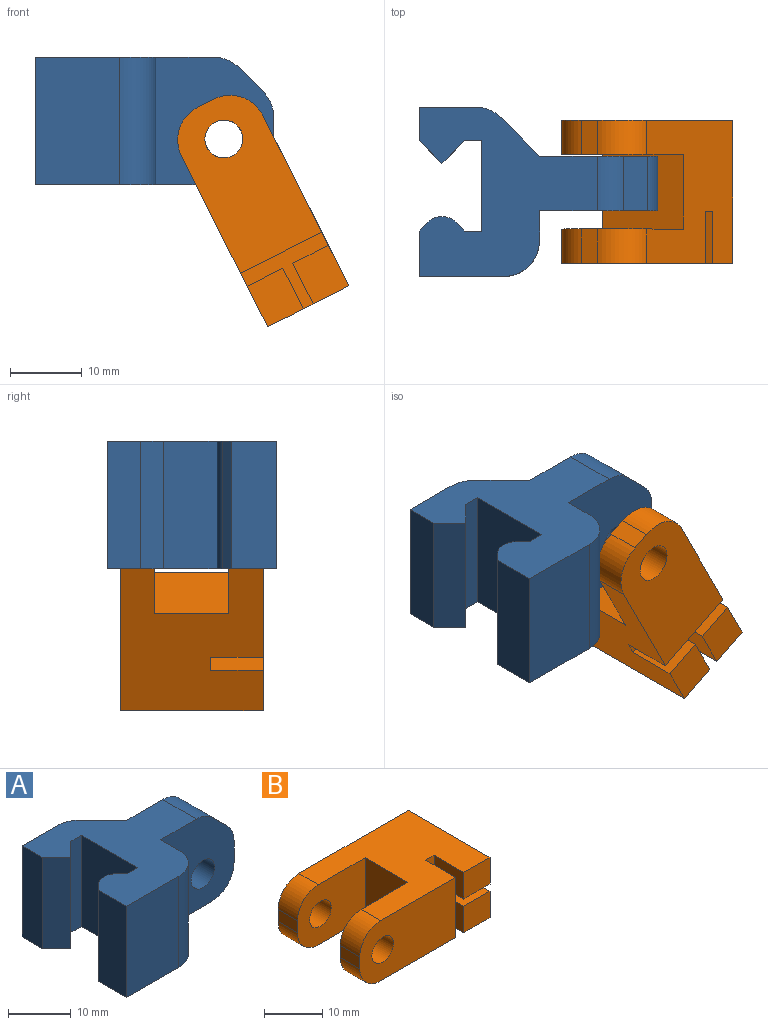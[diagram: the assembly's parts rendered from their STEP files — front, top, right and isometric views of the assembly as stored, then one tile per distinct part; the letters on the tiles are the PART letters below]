
ASSEMBLY  parts=2 mates=1
PART A: 26 faces, bbox 33.3x23.6x17.8 mm
  f0: plane 17.78x6.35mm, normal (-1,0,0), area 112.9mm2, adj f1,f12,f13,f14
  f1: plane 17.78x11.73mm, normal (0,-1,0), area 208.6mm2, adj f0,f13,f14,f23
  f2: plane 17.78x4.11mm, normal (1,0,0), area 73.1mm2, adj f13,f14,f15,f23
  f3: plane 17.78x5.33mm, normal (0.71,0.71,0), area 133.9mm2, adj f13,f14,f16,f21
  f4: plane 17.78x7.89mm, normal (0,1,0), area 140.3mm2, adj f5,f13,f14,f21
  f5: plane 17.78x4.64mm, normal (-1,0,0), area 82.4mm2, adj f4,f6,f13,f14
  f6: plane 17.78x3.18mm, normal (-0.71,-0.71,0), area 80mm2, adj f5,f7,f13,f14
  f7: plane 17.78x3.18mm, normal (0.71,-0.71,0), area 80mm2, adj f6,f8,f13,f14
  f8: plane 17.78x2.38mm, normal (0,-1,0), area 42.3mm2, adj f7,f9,f13,f14
  f9: plane 17.78x12.64mm, normal (-1,0,0), area 224.7mm2, adj f8,f10,f13,f14
  f10: plane 17.78x2.38mm, normal (0,1,0), area 42.3mm2, adj f9,f11,f13,f14
  f11: plane 17.78x1.21mm, normal (0.71,0.71,0), area 30.3mm2, adj f10,f13,f14,f20
  f12: plane 17.78x1.21mm, normal (-0.71,0.71,0), area 30.3mm2, adj f0,f13,f14,f20
  f13: plane 24.87x23.62mm, normal (0,0,1), area 337.2mm2, adj f0,f1,f2,f3,f4,f5,f6,f7
  f14: plane 28.24x23.62mm, normal (0,0,-1), area 362.9mm2, adj f0,f1,f2,f3,f4,f5,f6,f7
  f15: plane 17.78x16.51mm, normal (0,-1,0), area 244.7mm2, adj f2,f13,f14,f17,f18,f19,f22,f24
  f16: plane 17.78x16.51mm, normal (0,1,0), area 244.7mm2, adj f3,f13,f14,f17,f18,f19,f22,f24
  f17: plane 7.62x4.25mm, normal (1,0,0), area 32.4mm2, adj f15,f16,f22,f25
  f18: plane 7.62x3.37mm, normal (0.71,0,0.71), area 36.4mm2, adj f15,f16,f24,f25
  f19: cylinder r=2.65mm len=7.62mm, axis (0,-1,0), area 126.9mm2, adj f15,f16
  f20: cylinder r=2.79mm len=17.78mm, axis (0,0,-1), area 78mm2, adj f11,f12,f13,f14
  f21: cylinder r=5.08mm len=17.78mm, axis (0,0,-1), area 70.9mm2, adj f3,f4,f13,f14
  f22: cylinder r=5.08mm len=7.62mm, axis (0,1,0), area 60.8mm2, adj f14,f15,f16,f17
  f23: cylinder r=5.08mm len=17.78mm, axis (0,0,1), area 141.9mm2, adj f1,f2,f13,f14
  f24: cylinder r=5.08mm len=7.62mm, axis (0,-1,0), area 30.4mm2, adj f13,f15,f16,f18
  f25: cylinder r=5.08mm len=7.62mm, axis (0,1,0), area 30.4mm2, adj f15,f16,f17,f18
PART B: 24 faces, bbox 31.8x19.9x12.7 mm
  f0: plane 23.37x12.7mm, normal (0,-1,0), area 263.6mm2, adj f2,f3,f5,f13,f15,f17,f18
  f1: plane 6.35x5.59mm, normal (0,-1,0), area 35.5mm2, adj f3,f7,f19,f21
  f2: plane 26.67x19.94mm, normal (0,0,1), area 397.9mm2, adj f0,f4,f6,f7,f8,f10,f11,f16
  f3: plane 26.67x19.94mm, normal (0,0,-1), area 397.9mm2, adj f0,f1,f4,f7,f8,f10,f11,f14
  f4: plane 16.51x12.7mm, normal (0,1,0), area 176.5mm2, adj f2,f3,f5,f11,f13,f15,f17
  f5: plane 4.76x2.54mm, normal (-1,0,0), area 12.1mm2, adj f0,f4,f15,f17
  f6: plane 6.35x5.59mm, normal (0,-1,0), area 35.5mm2, adj f2,f7,f22,f23
  f7: plane 19.94x12.7mm, normal (1,0,0), area 242.1mm2, adj f1,f2,f3,f6,f8,f20,f21,f22
  f8: plane 31.75x12.7mm, normal (0,1,0), area 370.1mm2, adj f2,f3,f7,f9,f12,f14,f16
  f9: plane 4.76x2.54mm, normal (-1,0,0), area 12.1mm2, adj f8,f10,f14,f16
  f10: plane 16.51x12.7mm, normal (0,-1,0), area 176.5mm2, adj f2,f3,f9,f11,f12,f14,f16
  f11: plane 12.7x10.41mm, normal (-1,0,0), area 132.3mm2, adj f2,f3,f4,f10
  f12: cylinder r=2.65mm len=5.3mm, axis (0,-1,0), area 79.3mm2, adj f8,f10
  f13: cylinder r=2.65mm len=5.3mm, axis (0,-1,0), area 79.3mm2, adj f0,f4
  f14: cylinder r=5.08mm len=5.08mm, axis (0,-1,0), area 38mm2, adj f3,f8,f9,f10
  f15: cylinder r=5.08mm len=5.08mm, axis (0,-1,0), area 38mm2, adj f0,f3,f4,f5
  f16: cylinder r=5.08mm len=5.08mm, axis (0,1,0), area 38mm2, adj f2,f8,f9,f10
  f17: cylinder r=5.08mm len=5.08mm, axis (0,1,0), area 38mm2, adj f0,f2,f4,f5
  f18: plane 12.7x7.29mm, normal (1,0,0), area 92.6mm2, adj f0,f2,f3,f20
  f19: plane 7.29x5.59mm, normal (-1,0,0), area 40.7mm2, adj f1,f3,f20,f21
  f20: plane 12.7x8.38mm, normal (0,-1,0), area 35.5mm2, adj f2,f3,f7,f18,f19,f21,f22,f23
  f21: plane 7.29x6.35mm, normal (0,0,1), area 46.3mm2, adj f1,f7,f19,f20
  f22: plane 7.29x6.35mm, normal (0,0,-1), area 46.3mm2, adj f6,f7,f20,f23
  f23: plane 7.29x5.59mm, normal (-1,0,0), area 40.7mm2, adj f2,f6,f20,f22
PLACE A t=(-29.81,3.76,-2.28)mm fixed
PLACE B rot(axis=(0,1,0),63.2deg) t=(-14.85,-7.55,6.2)mm
MATE revolute B.f12 <-> A.f19  axis (0,-1,0) through (-6.66,2.87,4.07)mm
